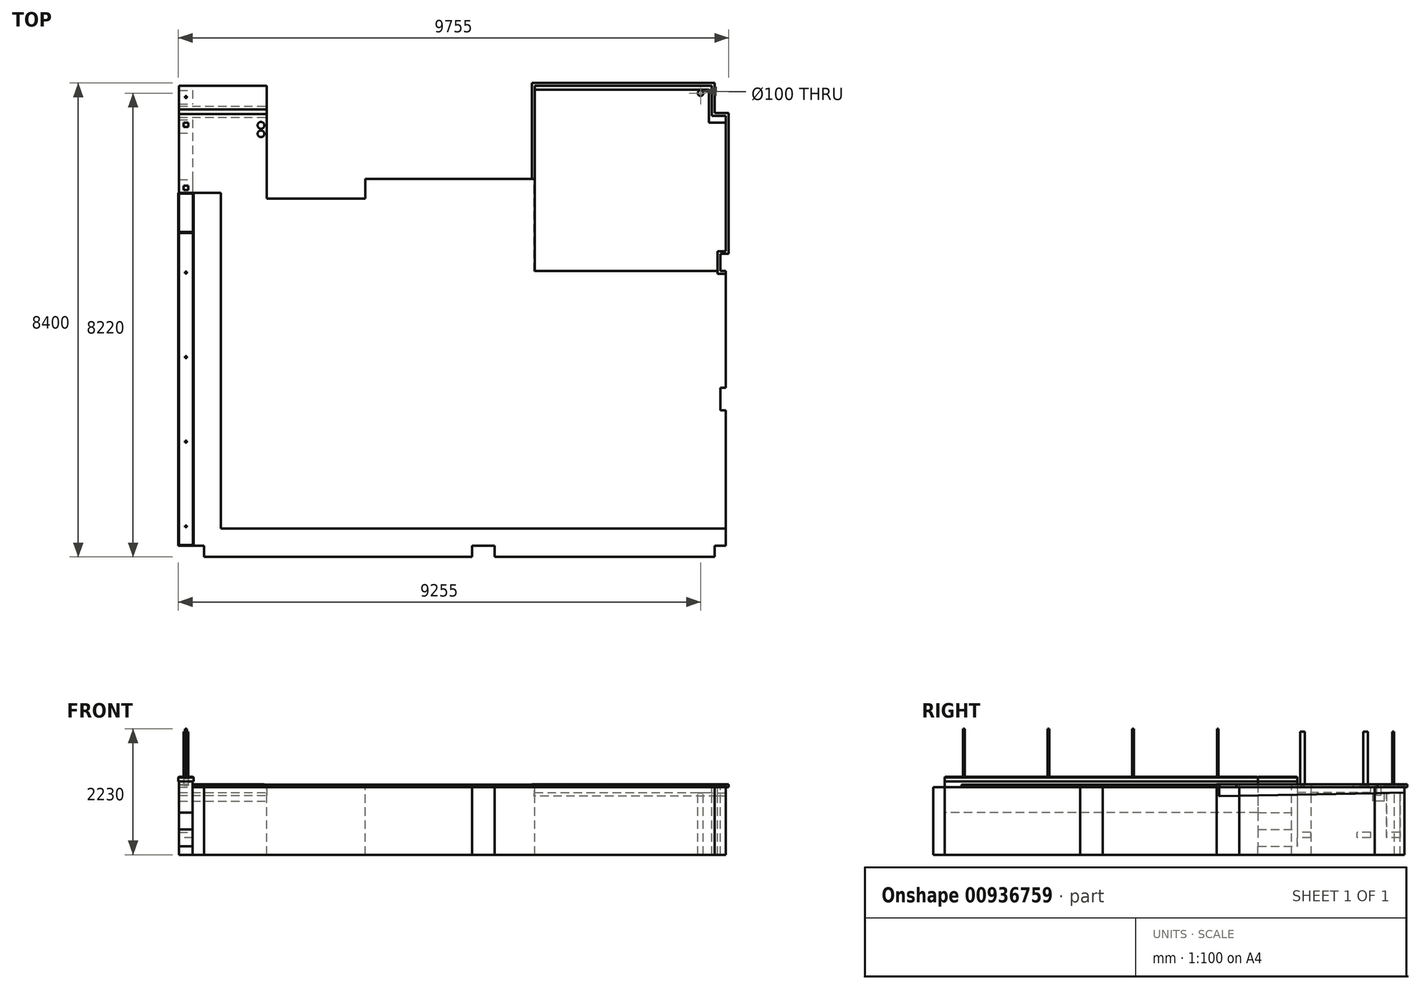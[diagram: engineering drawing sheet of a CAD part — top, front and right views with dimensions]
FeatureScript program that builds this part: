
annotation { "Feature Type Name" : "Feature", "Feature Type Description" : "" }
export const myFeature = defineFeature(function(context is Context, id is Id, definition is map)
    precondition{}
    {
        {
            var Q0;
            Q0=qCreatedBy(makeId("Top.planeOp"),FACE);
            var sketch = newSketch(context, id + "F0", { "sketchPlane" : qUnion([Q0])});
            skLineSegment(sketch, "E0", {"start": v(-250, 0) * mm, "end": v(0, 0) * mm, "construction": true});
            skLineSegment(sketch, "E1", {"start": v(0, 0) * mm, "end": v(0, -530) * mm, "construction": true});
            skCircle(sketch, "E2", {"center": v(-450, -130) * mm, "radius": 50 * mm});
            skLineSegment(sketch, "E3", {"start": v(-250, 0) * mm, "end": v(-250, -530) * mm});
            skLineSegment(sketch, "E4", {"start": v(-250, -530) * mm, "end": v(0, -530) * mm});
            skLineSegment(sketch, "E5", {"start": v(-250, 0) * mm, "end": v(-3390, 0) * mm});
            skLineSegment(sketch, "E6", {"start": v(0, -530) * mm, "end": v(0, -2930) * mm});
            skLineSegment(sketch, "E7", {"start": v(-3390, 0) * mm, "end": v(-3390, -1650) * mm});
            skLineSegment(sketch, "E8", {"start": v(0, -2930) * mm, "end": v(-150, -2930) * mm});
            skLineSegment(sketch, "E9", {"start": v(-150, -2930) * mm, "end": v(-150, -3330) * mm});
            skLineSegment(sketch, "E10", {"start": v(-150, -3330) * mm, "end": v(0, -3330) * mm});
            skLineSegment(sketch, "E11", {"start": v(-3390, -70) * mm, "end": v(-250, -70) * mm, "construction": true});
            skLineSegment(sketch, "E12", {"start": v(-300, -70) * mm, "end": v(-300, -650) * mm, "construction": true});
            skLineSegment(sketch, "E13", {"start": v(-300, -650) * mm, "end": v(0, -650) * mm, "construction": true});
            skLineSegment(sketch, "E14", {"start": v(-3390, -1650) * mm, "end": v(-6390, -1650) * mm});
            skLineSegment(sketch, "E15", {"start": v(-6390, -1650) * mm, "end": v(-6390, -2000) * mm});
            skLineSegment(sketch, "E16", {"start": v(-6390, -2000) * mm, "end": v(-8140, -2000) * mm});
            skLineSegment(sketch, "E17", {"start": v(-8140, -2000) * mm, "end": v(-8140, 0) * mm});
            skLineSegment(sketch, "E18", {"start": v(-8140, 0) * mm, "end": v(-9690, 0) * mm});
            skLineSegment(sketch, "E19", {"start": v(-9690, 0) * mm, "end": v(-9690, -2600) * mm});
            skLineSegment(sketch, "E20", {"start": v(-9450, -2600) * mm, "end": v(-9450, -8150) * mm});
            skLineSegment(sketch, "E21", {"start": v(-9450, -8150) * mm, "end": v(-9250, -8150) * mm});
            skLineSegment(sketch, "E22", {"start": v(-9250, -8150) * mm, "end": v(-9250, -8350) * mm});
            skLineSegment(sketch, "E23", {"start": v(-9250, -8350) * mm, "end": v(-4500, -8350) * mm});
            skLineSegment(sketch, "E24", {"start": v(-4500, -8350) * mm, "end": v(-4500, -8150) * mm});
            skLineSegment(sketch, "E25", {"start": v(-4500, -8150) * mm, "end": v(-4100, -8150) * mm});
            skLineSegment(sketch, "E26", {"start": v(0, -3330) * mm, "end": v(0, -5350) * mm});
            skLineSegment(sketch, "E27", {"start": v(0, -5350) * mm, "end": v(-100, -5350) * mm});
            skLineSegment(sketch, "E28", {"start": v(-100, -5350) * mm, "end": v(-100, -5750) * mm});
            skLineSegment(sketch, "E29", {"start": v(-100, -5750) * mm, "end": v(0, -5750) * mm});
            skLineSegment(sketch, "E30", {"start": v(0, -5750) * mm, "end": v(0, -8150) * mm});
            skLineSegment(sketch, "E31", {"start": v(0, -8150) * mm, "end": v(-200, -8150) * mm});
            skLineSegment(sketch, "E32", {"start": v(-200, -8150) * mm, "end": v(-200, -8350) * mm});
            skLineSegment(sketch, "E33", {"start": v(-200, -8350) * mm, "end": v(-4100, -8350) * mm});
            skLineSegment(sketch, "E34", {"start": v(-4100, -8150) * mm, "end": v(-4100, -8350) * mm});
            skLineSegment(sketch, "E35", {"start": v(-9690, -2600) * mm, "end": v(-9450, -2600) * mm});
            skSolve(sketch);
        }
        {
            var Q0;
            Q0=qCreatedBy(makeId("Top.planeOp"),FACE);
            var sketch = newSketch(context, id + "F1", { "sketchPlane" : qUnion([Q0])});
            skLineSegment(sketch, "E36.0", {"start": v(-3390, 0) * mm, "end": v(-3390, -1650) * mm});
            skLineSegment(sketch, "E36.1", {"start": v(-250, 0) * mm, "end": v(-3390, 0) * mm});
            skLineSegment(sketch, "E36.2", {"start": v(-250, 0) * mm, "end": v(-250, -530) * mm});
            skLineSegment(sketch, "E36.3", {"start": v(-250, -530) * mm, "end": v(0, -530) * mm});
            skLineSegment(sketch, "E36.4", {"start": v(0, -530) * mm, "end": v(0, -2930) * mm});
            skLineSegment(sketch, "E36.5", {"start": v(0, -2930) * mm, "end": v(-150, -2930) * mm});
            skLineSegment(sketch, "E36.6", {"start": v(-150, -2930) * mm, "end": v(-150, -3330) * mm});
            skLineSegment(sketch, "E36.7", {"start": v(-150, -3330) * mm, "end": v(0, -3330) * mm});
            skLineSegment(sketch, "E37.0", {"start": v(-3440, 50) * mm, "end": v(-3440, -1650) * mm});
            skLineSegment(sketch, "E37.1", {"start": v(-200, 50) * mm, "end": v(-3440, 50) * mm});
            skLineSegment(sketch, "E37.2", {"start": v(-200, 50) * mm, "end": v(-200, -480) * mm});
            skLineSegment(sketch, "E37.3", {"start": v(-200, -480) * mm, "end": v(50, -480) * mm});
            skLineSegment(sketch, "E37.4", {"start": v(-100, -3280) * mm, "end": v(0, -3280) * mm});
            skLineSegment(sketch, "E37.5", {"start": v(-100, -2980) * mm, "end": v(-100, -3280) * mm});
            skLineSegment(sketch, "E37.6", {"start": v(50, -2980) * mm, "end": v(-100, -2980) * mm});
            skLineSegment(sketch, "E37.7", {"start": v(50, -480) * mm, "end": v(50, -2980) * mm});
            skLineSegment(sketch, "E38", {"start": v(-3390, -1650) * mm, "end": v(-3440, -1650) * mm});
            skLineSegment(sketch, "E39", {"start": v(0, -3330) * mm, "end": v(0, -3280) * mm});
            skCircle(sketch, "E40.0", {"center": v(-450, -130) * mm, "radius": 50 * mm});
            skSolve(sketch);
        }
        {
            var Q0;
            Q0=qSketchRegion(id+"F1",true);
            extrude(context, id + "F2", {"entities" : qUnion([Q0]), "depth" : 50 * mm, "offsetDistance" : 25 * mm});
        }
        {
            var Q0;
            Q0=qCreatedBy(makeId("Top.planeOp"),FACE);
            var sketch = newSketch(context, id + "F3", { "sketchPlane" : qUnion([Q0])});
            skLineSegment(sketch, "E41.0", {"start": v(-3390, -70) * mm, "end": v(-300, -70) * mm});
            skLineSegment(sketch, "E41.1", {"start": v(-250, 0) * mm, "end": v(-3390, 0) * mm});
            skLineSegment(sketch, "E41.2", {"start": v(-3390, 0) * mm, "end": v(-3390, -70) * mm});
            skLineSegment(sketch, "E41.3", {"start": v(-300, -70) * mm, "end": v(-300, -650) * mm});
            skLineSegment(sketch, "E41.4", {"start": v(-250, 0) * mm, "end": v(-250, -530) * mm});
            skLineSegment(sketch, "E41.5", {"start": v(-300, -650) * mm, "end": v(0, -650) * mm});
            skLineSegment(sketch, "E41.6", {"start": v(-250, -530) * mm, "end": v(0, -530) * mm});
            skLineSegment(sketch, "E41.7", {"start": v(0, -530) * mm, "end": v(0, -650) * mm});
            skPoint(sketch, "E42.orphan", {"position": v(-250, -70) * mm});
            skPoint(sketch, "E43.orphan", {"position": v(0, -2930) * mm});
            skPoint(sketch, "E44.orphan", {"position": v(-3390, -1650) * mm});
            skSolve(sketch);
        }
        {
            var Q0;
            Q0=qSketchRegion(id+"F3",true);
            extrude(context, id + "F4", {"entities" : qUnion([Q0]), "depth" : 1 * mm, "offsetDistance" : 25 * mm});
        }
        {
            var Q0;
            Q0 = qSketchRegion(id + "F0", true);
            extrude(context, id + "F5", {"entities" : qUnion([Q0]), "oppositeDirection" : true, "depth" : 1200 * mm, "offsetDistance" : 25 * mm});
        }
        {
            var Q0;
            Q0=qCreatedBy(makeId("Top.planeOp"),FACE);
            var sketch = newSketch(context, id + "F6", { "sketchPlane" : qUnion([Q0])});
            skLineSegment(sketch, "E45.bottom", {"start": v(-9690, -2600) * mm, "end": v(-9450, -2600) * mm});
            skLineSegment(sketch, "E45.top", {"start": v(-9690, -8150) * mm, "end": v(-9450, -8150) * mm});
            skLineSegment(sketch, "E45.left", {"start": v(-9690, -2600) * mm, "end": v(-9690, -8150) * mm});
            skLineSegment(sketch, "E45.right", {"start": v(-9450, -2600) * mm, "end": v(-9450, -8150) * mm});
            skSolve(sketch);
        }
        {
            var Q0;
            Q0 = qSketchRegion(id + "F6", true);
            extrude(context, id + "F7", {"entities" : qUnion([Q0]), "depth" : 100 * mm, "offsetDistance" : 25 * mm, "hasSecondDirection" : true, "secondDirectionOppositeDirection" : true, "secondDirectionDepth" : 450 * mm});
        }
        {
            var Q0;
            Q0=makeQuery(id+"F0.imprint","IMPRINT",FACE,{"disambiguationData":[TD([[makeQuery(id+"F0.imprint","IMPRINT",EDGE,{"derivedFrom":sQuery(id+"F0.wireOp",EDGE,"E2")}),-1.0]])]});
            var sketch = newSketch(context, id + "F8", { "sketchPlane" : qUnion([Q0])});
            skLineSegment(sketch, "E46", {"start": v(-3390, -1650) * mm, "end": v(-3390, -3282) * mm});
            skLineSegment(sketch, "E47", {"start": v(-3390, -3282) * mm, "end": v(-150, -3282) * mm});
            skLineSegment(sketch, "E48.0", {"start": v(-150, -2930) * mm, "end": v(-150, -3282) * mm});
            skLineSegment(sketch, "E48.1", {"start": v(0, -2930) * mm, "end": v(-150, -2930) * mm});
            skLineSegment(sketch, "E48.2", {"start": v(0, -530) * mm, "end": v(0, -2930) * mm});
            skLineSegment(sketch, "E48.3", {"start": v(-250, -530) * mm, "end": v(0, -530) * mm});
            skLineSegment(sketch, "E48.4", {"start": v(-250, 0) * mm, "end": v(-250, -530) * mm});
            skLineSegment(sketch, "E48.5", {"start": v(-250, 0) * mm, "end": v(-3390, 0) * mm});
            skLineSegment(sketch, "E49.0", {"start": v(-3390, 0) * mm, "end": v(-3390, -1650) * mm});
            skSolve(sketch);
        }
        {
            var Q0;
            Q0=makeQuery(id+"F5.opExtrude","SWEPT_FACE",FACE,{"disambiguationData":[OSD([sQuery(id+"F0.wireOp",EDGE,"E9")])]});
            var sketch = newSketch(context, id + "F9", { "sketchPlane" : qUnion([Q0])});
            skLineSegment(sketch, "E50", {"start": v(-3282, 0) * mm, "end": v(-3282, -160) * mm});
            skLineSegment(sketch, "E51", {"start": v(-3282, -160) * mm, "end": v(0, -100) * mm});
            skLineSegment(sketch, "E52", {"start": v(0, -100) * mm, "end": v(0, 0) * mm});
            skSolve(sketch);
        }
        {
            var Q0;
            Q0=sQuery(id+"F9.wireOp",EDGE,"E51");
            cPlane(context, id + "F10", {"entities" : qUnion([Q0]), "cplaneType" : CPlaneType.LINE_ANGLE, "offset" : 25 * mm, "angle" : 0 * degree, "width" : 150 * mm, "height" : 150 * mm});
        }
        {
            var Q0;
            Q0 = qSketchRegion(id + "F8", true);
            var Q1;
            Q1=qCreatedBy(id+"F10.planeOp",FACE);
            var Q2;
            Q2=makeQuery(id+"F5.opExtrude","CAP_VERTEX",VERTEX,{"disambiguationData":[OSD([sQuery(id+"F0.wireOp",EDGE,"E6"),sQuery(id+"F0.wireOp",EDGE,"E8")])],"isStart":false});
            extrude(context, id + "F11", {"entities" : qUnion([Q0]), "operationType" : NewBodyOperationType.REMOVE, "endBound" : BoundingType.UP_TO_SURFACE, "oppositeDirection" : true, "depth" : 360 * mm, "endBoundEntityFace" : qUnion([Q1]), "endBoundEntityVertex" : qUnion([Q2]), "offsetDistance" : 25 * mm, "hasDraft" : true, "draftAngle" : 3 * degree});
        }
        {
            var Q0;
            Q0 = qSketchRegion(id + "F8", true);
            var Q1;
            Q1=makeQuery(id+"F11.boolean.opBoolean","COPY",FACE,{"derivedFrom":makeQuery(id+"F11.opExtrude","CAP_FACE",FACE,{"disambiguationData":[OSD([sQuery(id+"F8.wireOp",EDGE,"E46"),sQuery(id+"F8.wireOp",EDGE,"E47"),sQuery(id+"F8.wireOp",EDGE,"E48.0"),sQuery(id+"F8.wireOp",EDGE,"E48.1"),sQuery(id+"F8.wireOp",EDGE,"E48.2"),sQuery(id+"F8.wireOp",EDGE,"E48.3"),sQuery(id+"F8.wireOp",EDGE,"E48.4"),sQuery(id+"F8.wireOp",EDGE,"E48.5"),sQuery(id+"F8.wireOp",EDGE,"E49.0")])],"isStart":false})});
            extrude(context, id + "F12", {"entities" : qUnion([Q0]), "endBound" : BoundingType.UP_TO_SURFACE, "oppositeDirection" : true, "depth" : 25 * mm, "endBoundEntityFace" : qUnion([Q1]), "offsetDistance" : 25 * mm});
        }
        {
            var Q0;
            Q0=makeQuery(id+"F5.opExtrude","CAP_FACE",FACE,{"disambiguationData":[OSD([sQuery(id+"F0.wireOp",EDGE,"E2"),sQuery(id+"F0.wireOp",EDGE,"E3"),sQuery(id+"F0.wireOp",EDGE,"E4"),sQuery(id+"F0.wireOp",EDGE,"E5"),sQuery(id+"F0.wireOp",EDGE,"E6"),sQuery(id+"F0.wireOp",EDGE,"E7"),sQuery(id+"F0.wireOp",EDGE,"E8"),sQuery(id+"F0.wireOp",EDGE,"E9"),sQuery(id+"F0.wireOp",EDGE,"E10"),sQuery(id+"F0.wireOp",EDGE,"E14"),sQuery(id+"F0.wireOp",EDGE,"E15"),sQuery(id+"F0.wireOp",EDGE,"E16"),sQuery(id+"F0.wireOp",EDGE,"E17"),sQuery(id+"F0.wireOp",EDGE,"E18"),sQuery(id+"F0.wireOp",EDGE,"E19"),sQuery(id+"F0.wireOp",EDGE,"b0Gpvn7v-ytsP-87oV-qQFu-qrhvEngnIZt2"),sQuery(id+"F0.wireOp",EDGE,"E20"),sQuery(id+"F0.wireOp",EDGE,"E21"),sQuery(id+"F0.wireOp",EDGE,"E22"),sQuery(id+"F0.wireOp",EDGE,"E23"),sQuery(id+"F0.wireOp",EDGE,"E24"),sQuery(id+"F0.wireOp",EDGE,"E25"),sQuery(id+"F0.wireOp",EDGE,"E26"),sQuery(id+"F0.wireOp",EDGE,"E27"),sQuery(id+"F0.wireOp",EDGE,"E28"),sQuery(id+"F0.wireOp",EDGE,"E29"),sQuery(id+"F0.wireOp",EDGE,"E30"),sQuery(id+"F0.wireOp",EDGE,"E31"),sQuery(id+"F0.wireOp",EDGE,"E32"),sQuery(id+"F0.wireOp",EDGE,"E33"),sQuery(id+"F0.wireOp",EDGE,"E34")])],"isStart":true});
            var sketch = newSketch(context, id + "F13", { "sketchPlane" : qUnion([Q0])});
            skLineSegment(sketch, "E53.bottom", {"start": v(-9690, -360) * mm, "end": v(-8140, -360) * mm});
            skLineSegment(sketch, "E53.top", {"start": v(-9690, -560) * mm, "end": v(-8140, -560) * mm});
            skLineSegment(sketch, "E53.left", {"start": v(-9690, -360) * mm, "end": v(-9690, -560) * mm});
            skLineSegment(sketch, "E53.right", {"start": v(-8140, -360) * mm, "end": v(-8140, -560) * mm});
            skLineSegment(sketch, "E54", {"start": v(-9690, -420) * mm, "end": v(-8140, -420) * mm, "construction": true});
            skLineSegment(sketch, "E55", {"start": v(-9690, -500) * mm, "end": v(-8140, -500) * mm, "construction": true});
            skLineSegment(sketch, "E56", {"start": v(-8915, -360) * mm, "end": v(-8915, -420) * mm, "construction": true});
            skLineSegment(sketch, "E57", {"start": v(-8915, -420) * mm, "end": v(-8915, -500) * mm, "construction": true});
            skLineSegment(sketch, "E58", {"start": v(-8915, -500) * mm, "end": v(-8915, -560) * mm, "construction": true});
            skSolve(sketch);
        }
        {
            var Q0;
            Q0 = qSketchRegion(id + "F13", true);
            extrude(context, id + "F14", {"entities" : qUnion([Q0]), "operationType" : NewBodyOperationType.REMOVE, "oppositeDirection" : true, "depth" : 250 * mm, "offsetDistance" : 25 * mm});
        }
        {
            var Q0;
            {var subQ0=sQuery(id+"F0.wireOp",EDGE,"E17");var subQ1=sQuery(id+"F0.wireOp",EDGE,"E18");var subQ2=sQuery(id+"F0.wireOp",EDGE,"E19");Q0=makeQuery(id+"F14.boolean.opBoolean","SPLIT",FACE,{"disambiguationData":[TD([makeQuery(id+"F5.opExtrude","SWEPT_FACE",FACE,{"disambiguationData":[OSD([subQ1])]})])],"derivedFrom":makeQuery(id+"F5.opExtrude","CAP_FACE",FACE,{"disambiguationData":[OSD([sQuery(id+"F0.wireOp",EDGE,"E2"),sQuery(id+"F0.wireOp",EDGE,"E3"),sQuery(id+"F0.wireOp",EDGE,"E4"),sQuery(id+"F0.wireOp",EDGE,"E5"),sQuery(id+"F0.wireOp",EDGE,"E6"),sQuery(id+"F0.wireOp",EDGE,"E7"),sQuery(id+"F0.wireOp",EDGE,"E8"),sQuery(id+"F0.wireOp",EDGE,"E9"),sQuery(id+"F0.wireOp",EDGE,"E10"),sQuery(id+"F0.wireOp",EDGE,"E14"),sQuery(id+"F0.wireOp",EDGE,"E15"),sQuery(id+"F0.wireOp",EDGE,"E16"),subQ0,subQ1,subQ2,sQuery(id+"F0.wireOp",EDGE,"b0Gpvn7v-ytsP-87oV-qQFu-qrhvEngnIZt2"),sQuery(id+"F0.wireOp",EDGE,"E20"),sQuery(id+"F0.wireOp",EDGE,"E21"),sQuery(id+"F0.wireOp",EDGE,"E22"),sQuery(id+"F0.wireOp",EDGE,"E23"),sQuery(id+"F0.wireOp",EDGE,"E24"),sQuery(id+"F0.wireOp",EDGE,"E25"),sQuery(id+"F0.wireOp",EDGE,"E26"),sQuery(id+"F0.wireOp",EDGE,"E27"),sQuery(id+"F0.wireOp",EDGE,"E28"),sQuery(id+"F0.wireOp",EDGE,"E29"),sQuery(id+"F0.wireOp",EDGE,"E30"),sQuery(id+"F0.wireOp",EDGE,"E31"),sQuery(id+"F0.wireOp",EDGE,"E32"),sQuery(id+"F0.wireOp",EDGE,"E33"),sQuery(id+"F0.wireOp",EDGE,"E34")])],"isStart":true})});}
            extrude(context, id + "F15", {"entities" : qUnion([Q0]), "operationType" : NewBodyOperationType.REMOVE, "oppositeDirection" : true, "depth" : 100 * mm, "offsetDistance" : 25 * mm});
        }
        {
            var Q0;
            {var subQ0=sQuery(id+"F0.wireOp",EDGE,"E34");var subQ1=sQuery(id+"F0.wireOp",EDGE,"E33");var subQ2=sQuery(id+"F0.wireOp",EDGE,"E32");var subQ3=sQuery(id+"F0.wireOp",EDGE,"E31");var subQ4=sQuery(id+"F0.wireOp",EDGE,"E30");var subQ5=sQuery(id+"F0.wireOp",EDGE,"E29");var subQ6=sQuery(id+"F0.wireOp",EDGE,"E28");var subQ7=sQuery(id+"F0.wireOp",EDGE,"E27");var subQ8=sQuery(id+"F0.wireOp",EDGE,"E26");var subQ9=sQuery(id+"F0.wireOp",EDGE,"E25");var subQ10=sQuery(id+"F0.wireOp",EDGE,"E24");var subQ11=sQuery(id+"F0.wireOp",EDGE,"E23");var subQ12=sQuery(id+"F0.wireOp",EDGE,"E15");var subQ13=sQuery(id+"F0.wireOp",EDGE,"E14");var subQ14=sQuery(id+"F0.wireOp",EDGE,"E10");var subQ15=sQuery(id+"F0.wireOp",EDGE,"E9");var subQ16=sQuery(id+"F0.wireOp",EDGE,"E16");var subQ17=sQuery(id+"F0.wireOp",EDGE,"E17");var subQ18=sQuery(id+"F0.wireOp",EDGE,"E19");var subQ19=sQuery(id+"F0.wireOp",EDGE,"E20");var subQ20=sQuery(id+"F0.wireOp",EDGE,"E21");var subQ21=sQuery(id+"F0.wireOp",EDGE,"E22");var subQ22=sQuery(id+"F0.wireOp",EDGE,"E35");Q0=makeQuery(id+"F14.boolean.opBoolean","SPLIT",FACE,{"disambiguationData":[TD([makeQuery(id+"F5.opExtrude","SWEPT_FACE",FACE,{"disambiguationData":[OSD([subQ15])]})])],"derivedFrom":makeQuery(id+"F5.opExtrude","CAP_FACE",FACE,{"disambiguationData":[OSD([sQuery(id+"F0.wireOp",EDGE,"E2"),sQuery(id+"F0.wireOp",EDGE,"E3"),sQuery(id+"F0.wireOp",EDGE,"E4"),sQuery(id+"F0.wireOp",EDGE,"E5"),sQuery(id+"F0.wireOp",EDGE,"E6"),sQuery(id+"F0.wireOp",EDGE,"E7"),sQuery(id+"F0.wireOp",EDGE,"E8"),subQ15,subQ14,subQ13,subQ12,subQ16,subQ17,sQuery(id+"F0.wireOp",EDGE,"E18"),subQ18,subQ19,subQ20,subQ21,subQ11,subQ10,subQ9,subQ8,subQ7,subQ6,subQ5,subQ4,subQ3,subQ2,subQ1,subQ0,subQ22])],"isStart":true})});}
            var sketch = newSketch(context, id + "F16", { "sketchPlane" : qUnion([Q0])});
            skLineSegment(sketch, "E59.bottom", {"start": v(-9450, -2600) * mm, "end": v(-9690, -2600) * mm});
            skLineSegment(sketch, "E59.top", {"start": v(-9450, -1900) * mm, "end": v(-9690, -1900) * mm});
            skLineSegment(sketch, "E59.left", {"start": v(-9450, -2600) * mm, "end": v(-9450, -1900) * mm});
            skLineSegment(sketch, "E59.right", {"start": v(-9690, -2600) * mm, "end": v(-9690, -1900) * mm});
            skSolve(sketch);
        }
        {
            var Q0;
            Q0 = qSketchRegion(id + "F16", true);
            extrude(context, id + "F17", {"entities" : qUnion([Q0]), "operationType" : NewBodyOperationType.REMOVE, "oppositeDirection" : true, "depth" : 1050 * mm, "offsetDistance" : 25 * mm});
        }
        {
            var Q0;
            {var subQ0=sQuery(id+"F0.wireOp",EDGE,"E34");var subQ1=sQuery(id+"F0.wireOp",EDGE,"E33");var subQ2=sQuery(id+"F0.wireOp",EDGE,"E32");var subQ3=sQuery(id+"F0.wireOp",EDGE,"E31");var subQ4=sQuery(id+"F0.wireOp",EDGE,"E30");var subQ5=sQuery(id+"F0.wireOp",EDGE,"E29");var subQ6=sQuery(id+"F0.wireOp",EDGE,"E28");var subQ7=sQuery(id+"F0.wireOp",EDGE,"E27");var subQ8=sQuery(id+"F0.wireOp",EDGE,"E26");var subQ9=sQuery(id+"F0.wireOp",EDGE,"E25");var subQ10=sQuery(id+"F0.wireOp",EDGE,"E24");var subQ11=sQuery(id+"F0.wireOp",EDGE,"E23");var subQ12=sQuery(id+"F0.wireOp",EDGE,"E15");var subQ13=sQuery(id+"F0.wireOp",EDGE,"E14");var subQ14=sQuery(id+"F0.wireOp",EDGE,"E10");var subQ15=sQuery(id+"F0.wireOp",EDGE,"E9");var subQ16=sQuery(id+"F0.wireOp",EDGE,"E16");var subQ17=sQuery(id+"F0.wireOp",EDGE,"E17");var subQ18=sQuery(id+"F0.wireOp",EDGE,"E19");var subQ19=sQuery(id+"F0.wireOp",EDGE,"E20");var subQ20=sQuery(id+"F0.wireOp",EDGE,"E21");var subQ21=sQuery(id+"F0.wireOp",EDGE,"E22");var subQ22=sQuery(id+"F0.wireOp",EDGE,"E35");Q0=makeQuery(id+"F14.boolean.opBoolean","SPLIT",FACE,{"disambiguationData":[TD([makeQuery(id+"F5.opExtrude","SWEPT_FACE",FACE,{"disambiguationData":[OSD([subQ15])]})])],"derivedFrom":makeQuery(id+"F5.opExtrude","CAP_FACE",FACE,{"disambiguationData":[OSD([sQuery(id+"F0.wireOp",EDGE,"E2"),sQuery(id+"F0.wireOp",EDGE,"E3"),sQuery(id+"F0.wireOp",EDGE,"E4"),sQuery(id+"F0.wireOp",EDGE,"E5"),sQuery(id+"F0.wireOp",EDGE,"E6"),sQuery(id+"F0.wireOp",EDGE,"E7"),sQuery(id+"F0.wireOp",EDGE,"E8"),subQ15,subQ14,subQ13,subQ12,subQ16,subQ17,sQuery(id+"F0.wireOp",EDGE,"E18"),subQ18,subQ19,subQ20,subQ21,subQ11,subQ10,subQ9,subQ8,subQ7,subQ6,subQ5,subQ4,subQ3,subQ2,subQ1,subQ0,subQ22])],"isStart":true})});}
            var sketch = newSketch(context, id + "F18", { "sketchPlane" : qUnion([Q0])});
            skLineSegment(sketch, "E60.bottom", {"start": v(-9690, -600) * mm, "end": v(-9450, -600) * mm});
            skLineSegment(sketch, "E60.top", {"start": v(-9690, -840) * mm, "end": v(-9450, -840) * mm});
            skLineSegment(sketch, "E60.left", {"start": v(-9690, -600) * mm, "end": v(-9690, -840) * mm});
            skLineSegment(sketch, "E60.right", {"start": v(-9450, -600) * mm, "end": v(-9450, -840) * mm});
            skLineSegment(sketch, "E61.bottom", {"start": v(-9690, -1660) * mm, "end": v(-9450, -1660) * mm});
            skLineSegment(sketch, "E61.top", {"start": v(-9690, -1900) * mm, "end": v(-9450, -1900) * mm});
            skLineSegment(sketch, "E61.left", {"start": v(-9690, -1660) * mm, "end": v(-9690, -1900) * mm});
            skLineSegment(sketch, "E61.right", {"start": v(-9450, -1660) * mm, "end": v(-9450, -1900) * mm});
            skSolve(sketch);
        }
        {
            var Q0;
            Q0 = qSketchRegion(id + "F18", true);
            extrude(context, id + "F19", {"entities" : qUnion([Q0]), "operationType" : NewBodyOperationType.REMOVE, "oppositeDirection" : true, "depth" : 900 * mm, "offsetDistance" : 25 * mm});
        }
        {
            var Q0;
            {var subQ0=sQuery(id+"F0.wireOp",EDGE,"E34");var subQ1=sQuery(id+"F0.wireOp",EDGE,"E33");var subQ2=sQuery(id+"F0.wireOp",EDGE,"E32");var subQ3=sQuery(id+"F0.wireOp",EDGE,"E31");var subQ4=sQuery(id+"F0.wireOp",EDGE,"E30");var subQ5=sQuery(id+"F0.wireOp",EDGE,"E29");var subQ6=sQuery(id+"F0.wireOp",EDGE,"E28");var subQ7=sQuery(id+"F0.wireOp",EDGE,"E27");var subQ8=sQuery(id+"F0.wireOp",EDGE,"E26");var subQ9=sQuery(id+"F0.wireOp",EDGE,"E25");var subQ10=sQuery(id+"F0.wireOp",EDGE,"E24");var subQ11=sQuery(id+"F0.wireOp",EDGE,"E23");var subQ12=sQuery(id+"F0.wireOp",EDGE,"E15");var subQ13=sQuery(id+"F0.wireOp",EDGE,"E14");var subQ14=sQuery(id+"F0.wireOp",EDGE,"E10");var subQ15=sQuery(id+"F0.wireOp",EDGE,"E9");var subQ16=sQuery(id+"F0.wireOp",EDGE,"E16");var subQ17=sQuery(id+"F0.wireOp",EDGE,"E17");var subQ18=sQuery(id+"F0.wireOp",EDGE,"E19");var subQ19=sQuery(id+"F0.wireOp",EDGE,"E20");var subQ20=sQuery(id+"F0.wireOp",EDGE,"E21");var subQ21=sQuery(id+"F0.wireOp",EDGE,"E22");var subQ22=sQuery(id+"F0.wireOp",EDGE,"E35");Q0=makeQuery(id+"F14.boolean.opBoolean","SPLIT",FACE,{"disambiguationData":[TD([makeQuery(id+"F5.opExtrude","SWEPT_FACE",FACE,{"disambiguationData":[OSD([subQ15])]})])],"derivedFrom":makeQuery(id+"F5.opExtrude","CAP_FACE",FACE,{"disambiguationData":[OSD([sQuery(id+"F0.wireOp",EDGE,"E2"),sQuery(id+"F0.wireOp",EDGE,"E3"),sQuery(id+"F0.wireOp",EDGE,"E4"),sQuery(id+"F0.wireOp",EDGE,"E5"),sQuery(id+"F0.wireOp",EDGE,"E6"),sQuery(id+"F0.wireOp",EDGE,"E7"),sQuery(id+"F0.wireOp",EDGE,"E8"),subQ15,subQ14,subQ13,subQ12,subQ16,subQ17,sQuery(id+"F0.wireOp",EDGE,"E18"),subQ18,subQ19,subQ20,subQ21,subQ11,subQ10,subQ9,subQ8,subQ7,subQ6,subQ5,subQ4,subQ3,subQ2,subQ1,subQ0,subQ22])],"isStart":true})});}
            var sketch = newSketch(context, id + "F20", { "sketchPlane" : qUnion([Q0])});
            skLineSegment(sketch, "E62.bottom", {"start": v(-9690, -840) * mm, "end": v(-9450, -840) * mm});
            skLineSegment(sketch, "E62.top", {"start": v(-9690, -1660) * mm, "end": v(-9450, -1660) * mm});
            skLineSegment(sketch, "E62.left", {"start": v(-9690, -840) * mm, "end": v(-9690, -1660) * mm});
            skLineSegment(sketch, "E62.right", {"start": v(-9450, -840) * mm, "end": v(-9450, -1660) * mm});
            skSolve(sketch);
        }
        {
            var Q0;
            Q0 = qSketchRegion(id + "F20", true);
            extrude(context, id + "F21", {"entities" : qUnion([Q0]), "operationType" : NewBodyOperationType.REMOVE, "oppositeDirection" : true, "depth" : 400 * mm, "offsetDistance" : 25 * mm});
        }
        {
            var Q0;
            {var subQ0=sQuery(id+"F0.wireOp",EDGE,"E34");var subQ1=sQuery(id+"F0.wireOp",EDGE,"E33");var subQ2=sQuery(id+"F0.wireOp",EDGE,"E32");var subQ3=sQuery(id+"F0.wireOp",EDGE,"E31");var subQ4=sQuery(id+"F0.wireOp",EDGE,"E30");var subQ5=sQuery(id+"F0.wireOp",EDGE,"E29");var subQ6=sQuery(id+"F0.wireOp",EDGE,"E28");var subQ7=sQuery(id+"F0.wireOp",EDGE,"E27");var subQ8=sQuery(id+"F0.wireOp",EDGE,"E26");var subQ9=sQuery(id+"F0.wireOp",EDGE,"E25");var subQ10=sQuery(id+"F0.wireOp",EDGE,"E24");var subQ11=sQuery(id+"F0.wireOp",EDGE,"E23");var subQ12=sQuery(id+"F0.wireOp",EDGE,"E15");var subQ13=sQuery(id+"F0.wireOp",EDGE,"E14");var subQ14=sQuery(id+"F0.wireOp",EDGE,"E10");var subQ15=sQuery(id+"F0.wireOp",EDGE,"E9");var subQ16=sQuery(id+"F0.wireOp",EDGE,"E16");var subQ17=sQuery(id+"F0.wireOp",EDGE,"E17");var subQ18=sQuery(id+"F0.wireOp",EDGE,"E19");var subQ19=sQuery(id+"F0.wireOp",EDGE,"E20");var subQ20=sQuery(id+"F0.wireOp",EDGE,"E21");var subQ21=sQuery(id+"F0.wireOp",EDGE,"E22");var subQ22=sQuery(id+"F0.wireOp",EDGE,"E35");Q0=makeQuery(id+"F14.boolean.opBoolean","SPLIT",FACE,{"disambiguationData":[TD([makeQuery(id+"F5.opExtrude","SWEPT_FACE",FACE,{"disambiguationData":[OSD([subQ15])]})])],"derivedFrom":makeQuery(id+"F5.opExtrude","CAP_FACE",FACE,{"disambiguationData":[OSD([sQuery(id+"F0.wireOp",EDGE,"E2"),sQuery(id+"F0.wireOp",EDGE,"E3"),sQuery(id+"F0.wireOp",EDGE,"E4"),sQuery(id+"F0.wireOp",EDGE,"E5"),sQuery(id+"F0.wireOp",EDGE,"E6"),sQuery(id+"F0.wireOp",EDGE,"E7"),sQuery(id+"F0.wireOp",EDGE,"E8"),subQ15,subQ14,subQ13,subQ12,subQ16,subQ17,sQuery(id+"F0.wireOp",EDGE,"E18"),subQ18,subQ19,subQ20,subQ21,subQ11,subQ10,subQ9,subQ8,subQ7,subQ6,subQ5,subQ4,subQ3,subQ2,subQ1,subQ0,subQ22])],"isStart":true})});}
            var sketch = newSketch(context, id + "F22", { "sketchPlane" : qUnion([Q0])});
            skLineSegment(sketch, "E63.bottom", {"start": v(-9690, -80) * mm, "end": v(-9450, -80) * mm});
            skLineSegment(sketch, "E63.top", {"start": v(-9690, -320) * mm, "end": v(-9450, -320) * mm});
            skLineSegment(sketch, "E63.left", {"start": v(-9690, -80) * mm, "end": v(-9690, -320) * mm});
            skLineSegment(sketch, "E63.right", {"start": v(-9450, -80) * mm, "end": v(-9450, -320) * mm});
            skLineSegment(sketch, "E64", {"start": v(-9690, -200) * mm, "end": v(-9450, -200) * mm, "construction": true});
            skSolve(sketch);
        }
        {
            var Q0;
            Q0 = qSketchRegion(id + "F22", true);
            extrude(context, id + "F23", {"entities" : qUnion([Q0]), "operationType" : NewBodyOperationType.REMOVE, "oppositeDirection" : true, "depth" : 900 * mm, "offsetDistance" : 25 * mm});
        }
        {
            var Q0;
            Q0=makeQuery(id+"F7.opExtrude","CAP_FACE",FACE,{"disambiguationData":[OSD([sQuery(id+"F6.wireOp",EDGE,"E45.bottom"),sQuery(id+"F6.wireOp",EDGE,"E45.top"),sQuery(id+"F6.wireOp",EDGE,"E45.left"),sQuery(id+"F6.wireOp",EDGE,"E45.right")])],"isStart":false});
            var sketch = newSketch(context, id + "F24", { "sketchPlane" : qUnion([Q0])});
            skLineSegment(sketch, "E65.bottom", {"start": v(-9705, -2600) * mm, "end": v(-9435, -2600) * mm});
            skLineSegment(sketch, "E65.top", {"start": v(-9705, -8150) * mm, "end": v(-9435, -8150) * mm});
            skLineSegment(sketch, "E65.left", {"start": v(-9705, -2600) * mm, "end": v(-9705, -8150) * mm});
            skLineSegment(sketch, "E65.right", {"start": v(-9435, -2600) * mm, "end": v(-9435, -8150) * mm});
            skLineSegment(sketch, "E66", {"start": v(-9570, -2600) * mm, "end": v(-9570, -8150) * mm, "construction": true});
            skSolve(sketch);
        }
        {
            var Q0;
            Q0 = qSketchRegion(id + "F24", true);
            extrude(context, id + "F25", {"entities" : qUnion([Q0]), "depth" : 80 * mm, "offsetDistance" : 25 * mm});
        }
        {
            var Q0;
            Q0=makeQuery(id+"F25.opExtrude","CAP_FACE",FACE,{"disambiguationData":[OSD([sQuery(id+"F24.wireOp",EDGE,"E65.bottom"),sQuery(id+"F24.wireOp",EDGE,"E65.top"),sQuery(id+"F24.wireOp",EDGE,"E65.left"),sQuery(id+"F24.wireOp",EDGE,"E65.right")])],"isStart":false});
            chamfer(context, id + "F26", {"entities" : qUnion([Q0]), "width" : 10 * mm, "tangentPropagation" : true});
        }
        {
            var Q0;
            Q0=makeQuery(id+"F17.boolean.opBoolean","COPY",FACE,{"derivedFrom":makeQuery(id+"F17.opExtrude","CAP_FACE",FACE,{"disambiguationData":[OSD([sQuery(id+"F16.wireOp",EDGE,"E59.bottom"),sQuery(id+"F16.wireOp",EDGE,"E59.top"),sQuery(id+"F16.wireOp",EDGE,"E59.left"),sQuery(id+"F16.wireOp",EDGE,"E59.right")])],"isStart":false})});
            extrude(context, id + "F27", {"entities" : qUnion([Q0]), "depth" : 300 * mm, "offsetDistance" : 25 * mm});
        }
        {
            var Q0;
            Q0=makeQuery(id+"F27.opExtrude","CAP_FACE",FACE,{"disambiguationData":[OSD([sQuery(id+"F16.wireOp",EDGE,"E59.bottom"),sQuery(id+"F16.wireOp",EDGE,"E59.top"),sQuery(id+"F16.wireOp",EDGE,"E59.left"),sQuery(id+"F16.wireOp",EDGE,"E59.right")])],"isStart":false});
            extrude(context, id + "F28", {"entities" : qUnion([Q0]), "depth" : 300 * mm, "offsetDistance" : 25 * mm});
        }
        {
            var Q0;
            Q0=makeQuery(id+"F19.boolean.opBoolean","COPY",FACE,{"derivedFrom":makeQuery(id+"F19.opExtrude","CAP_FACE",FACE,{"disambiguationData":[OSD([sQuery(id+"F18.wireOp",EDGE,"E61.bottom"),sQuery(id+"F18.wireOp",EDGE,"E61.top"),sQuery(id+"F18.wireOp",EDGE,"E61.left"),sQuery(id+"F18.wireOp",EDGE,"E61.right")])],"isStart":false})});
            var Q1;
            Q1=makeQuery(id+"F19.boolean.opBoolean","COPY",FACE,{"derivedFrom":makeQuery(id+"F19.opExtrude","CAP_FACE",FACE,{"disambiguationData":[OSD([sQuery(id+"F18.wireOp",EDGE,"E60.bottom"),sQuery(id+"F18.wireOp",EDGE,"E60.top"),sQuery(id+"F18.wireOp",EDGE,"E60.left"),sQuery(id+"F18.wireOp",EDGE,"E60.right")])],"isStart":false})});
            var Q2;
            Q2=makeQuery(id+"F23.boolean.opBoolean","COPY",FACE,{"derivedFrom":makeQuery(id+"F23.opExtrude","CAP_FACE",FACE,{"disambiguationData":[OSD([sQuery(id+"F22.wireOp",EDGE,"E63.bottom"),sQuery(id+"F22.wireOp",EDGE,"E63.top"),sQuery(id+"F22.wireOp",EDGE,"E63.left"),sQuery(id+"F22.wireOp",EDGE,"E63.right")])],"isStart":false})});
            extrude(context, id + "F29", {"entities" : qUnion([Q0, Q1, Q2]), "depth" : 100 * mm, "offsetDistance" : 25 * mm});
        }
        {
            var Q0;
            Q0=makeQuery(id+"F29.opExtrude","CAP_FACE",FACE,{"disambiguationData":[OSD([sQuery(id+"F18.wireOp",EDGE,"E61.bottom"),sQuery(id+"F18.wireOp",EDGE,"E61.top"),sQuery(id+"F18.wireOp",EDGE,"E61.left"),sQuery(id+"F18.wireOp",EDGE,"E61.right")])],"isStart":false});
            var Q1;
            Q1=makeQuery(id+"F29.opExtrude","CAP_FACE",FACE,{"disambiguationData":[OSD([sQuery(id+"F18.wireOp",EDGE,"E60.bottom"),sQuery(id+"F18.wireOp",EDGE,"E60.top"),sQuery(id+"F18.wireOp",EDGE,"E60.left"),sQuery(id+"F18.wireOp",EDGE,"E60.right")])],"isStart":false});
            var Q2;
            Q2=makeQuery(id+"F29.opExtrude","CAP_FACE",FACE,{"disambiguationData":[OSD([sQuery(id+"F22.wireOp",EDGE,"E63.bottom"),sQuery(id+"F22.wireOp",EDGE,"E63.top"),sQuery(id+"F22.wireOp",EDGE,"E63.left"),sQuery(id+"F22.wireOp",EDGE,"E63.right")])],"isStart":false});
            extrude(context, id + "F30", {"entities" : qUnion([Q0, Q1, Q2]), "depth" : 700 * mm, "offsetDistance" : 25 * mm});
        }
        {
            var Q0;
            Q0=makeQuery(id+"F21.boolean.opBoolean","COPY",FACE,{"derivedFrom":makeQuery(id+"F21.opExtrude","CAP_FACE",FACE,{"disambiguationData":[OSD([sQuery(id+"F20.wireOp",EDGE,"E62.bottom"),sQuery(id+"F20.wireOp",EDGE,"E62.top"),sQuery(id+"F20.wireOp",EDGE,"E62.left"),sQuery(id+"F20.wireOp",EDGE,"E62.right")])],"isStart":false})});
            var Q1;
            Q1=makeQuery(id+"F30.opExtrude","CAP_FACE",FACE,{"disambiguationData":[OSD([sQuery(id+"F18.wireOp",EDGE,"E61.bottom"),sQuery(id+"F18.wireOp",EDGE,"E61.top"),sQuery(id+"F18.wireOp",EDGE,"E61.left"),sQuery(id+"F18.wireOp",EDGE,"E61.right")])],"isStart":false});
            extrude(context, id + "F31", {"entities" : qUnion([Q0]), "operationType" : NewBodyOperationType.ADD, "endBound" : BoundingType.UP_TO_SURFACE, "depth" : 25 * mm, "endBoundEntityFace" : qUnion([Q1]), "offsetDistance" : 25 * mm});
        }
        {
            var Q0;
            Q0=makeQuery(id+"F28.opExtrude","CAP_FACE",FACE,{"disambiguationData":[OSD([sQuery(id+"F16.wireOp",EDGE,"E59.bottom"),sQuery(id+"F16.wireOp",EDGE,"E59.top"),sQuery(id+"F16.wireOp",EDGE,"E59.left"),sQuery(id+"F16.wireOp",EDGE,"E59.right")])],"isStart":false});
            var Q1;
            Q1=makeQuery(id+"F7.opExtrude","CAP_FACE",FACE,{"disambiguationData":[OSD([sQuery(id+"F6.wireOp",EDGE,"E45.bottom"),sQuery(id+"F6.wireOp",EDGE,"E45.top"),sQuery(id+"F6.wireOp",EDGE,"E45.left"),sQuery(id+"F6.wireOp",EDGE,"E45.right")])],"isStart":false});
            extrude(context, id + "F32", {"entities" : qUnion([Q0]), "endBound" : BoundingType.UP_TO_SURFACE, "depth" : 25 * mm, "endBoundEntityFace" : qUnion([Q1]), "offsetDistance" : 25 * mm});
        }
        {
            var Q0;
            Q0=makeQuery(id+"F32.opExtrude","CAP_FACE",FACE,{"disambiguationData":[OSD([sQuery(id+"F16.wireOp",EDGE,"E59.bottom"),sQuery(id+"F16.wireOp",EDGE,"E59.top"),sQuery(id+"F16.wireOp",EDGE,"E59.left"),sQuery(id+"F16.wireOp",EDGE,"E59.right")])],"isStart":false});
            var sketch = newSketch(context, id + "F33", { "sketchPlane" : qUnion([Q0])});
            skLineSegment(sketch, "E67.bottom", {"start": v(-9705, -2600) * mm, "end": v(-9435, -2600) * mm});
            skLineSegment(sketch, "E67.top", {"start": v(-9705, -1900) * mm, "end": v(-9435, -1900) * mm});
            skLineSegment(sketch, "E67.left", {"start": v(-9705, -1900) * mm, "end": v(-9705, -2600) * mm});
            skLineSegment(sketch, "E67.right", {"start": v(-9435, -1900) * mm, "end": v(-9435, -2600) * mm});
            skLineSegment(sketch, "E68", {"start": v(-9570, -1900) * mm, "end": v(-9570, -2600) * mm, "construction": true});
            skSolve(sketch);
        }
        {
            var Q0;
            Q0 = qSketchRegion(id + "F33", true);
            var Q1;
            Q1=makeQuery(id+"F25.opExtrude","CAP_FACE",FACE,{"disambiguationData":[OSD([sQuery(id+"F24.wireOp",EDGE,"E65.bottom"),sQuery(id+"F24.wireOp",EDGE,"E65.top"),sQuery(id+"F24.wireOp",EDGE,"E65.left"),sQuery(id+"F24.wireOp",EDGE,"E65.right")])],"isStart":false});
            extrude(context, id + "F34", {"entities" : qUnion([Q0]), "endBound" : BoundingType.UP_TO_SURFACE, "depth" : 25 * mm, "endBoundEntityFace" : qUnion([Q1]), "offsetDistance" : 25 * mm});
        }
        {
            var Q0;
            Q0=makeQuery(id+"F34.opExtrude","CAP_FACE",FACE,{"disambiguationData":[OSD([sQuery(id+"F33.wireOp",EDGE,"E67.bottom"),sQuery(id+"F33.wireOp",EDGE,"E67.top"),sQuery(id+"F33.wireOp",EDGE,"E67.left"),sQuery(id+"F33.wireOp",EDGE,"E67.right")])],"isStart":false});
            chamfer(context, id + "F35", {"entities" : qUnion([Q0]), "width" : 10 * mm, "tangentPropagation" : true});
        }
        {
            var Q0;
            {var subQ0=sQuery(id+"F0.wireOp",EDGE,"E34");var subQ1=sQuery(id+"F0.wireOp",EDGE,"E33");var subQ2=sQuery(id+"F0.wireOp",EDGE,"E32");var subQ3=sQuery(id+"F0.wireOp",EDGE,"E31");var subQ4=sQuery(id+"F0.wireOp",EDGE,"E30");var subQ5=sQuery(id+"F0.wireOp",EDGE,"E29");var subQ6=sQuery(id+"F0.wireOp",EDGE,"E28");var subQ7=sQuery(id+"F0.wireOp",EDGE,"E27");var subQ8=sQuery(id+"F0.wireOp",EDGE,"E26");var subQ9=sQuery(id+"F0.wireOp",EDGE,"E25");var subQ10=sQuery(id+"F0.wireOp",EDGE,"E24");var subQ11=sQuery(id+"F0.wireOp",EDGE,"E23");var subQ12=sQuery(id+"F0.wireOp",EDGE,"E15");var subQ13=sQuery(id+"F0.wireOp",EDGE,"E14");var subQ14=sQuery(id+"F0.wireOp",EDGE,"E10");var subQ15=sQuery(id+"F0.wireOp",EDGE,"E9");var subQ16=sQuery(id+"F0.wireOp",EDGE,"E16");var subQ17=sQuery(id+"F0.wireOp",EDGE,"E17");var subQ18=sQuery(id+"F0.wireOp",EDGE,"E19");var subQ19=sQuery(id+"F0.wireOp",EDGE,"E20");var subQ20=sQuery(id+"F0.wireOp",EDGE,"E21");var subQ21=sQuery(id+"F0.wireOp",EDGE,"E22");var subQ22=sQuery(id+"F0.wireOp",EDGE,"E35");Q0=makeQuery(id+"F14.boolean.opBoolean","SPLIT",FACE,{"disambiguationData":[TD([makeQuery(id+"F5.opExtrude","SWEPT_FACE",FACE,{"disambiguationData":[OSD([subQ15])]})])],"derivedFrom":makeQuery(id+"F5.opExtrude","CAP_FACE",FACE,{"disambiguationData":[OSD([sQuery(id+"F0.wireOp",EDGE,"E2"),sQuery(id+"F0.wireOp",EDGE,"E3"),sQuery(id+"F0.wireOp",EDGE,"E4"),sQuery(id+"F0.wireOp",EDGE,"E5"),sQuery(id+"F0.wireOp",EDGE,"E6"),sQuery(id+"F0.wireOp",EDGE,"E7"),sQuery(id+"F0.wireOp",EDGE,"E8"),subQ15,subQ14,subQ13,subQ12,subQ16,subQ17,sQuery(id+"F0.wireOp",EDGE,"E18"),subQ18,subQ19,subQ20,subQ21,subQ11,subQ10,subQ9,subQ8,subQ7,subQ6,subQ5,subQ4,subQ3,subQ2,subQ1,subQ0,subQ22])],"isStart":true})});}
            var sketch = newSketch(context, id + "F36", { "sketchPlane" : qUnion([Q0])});
            skLineSegment(sketch, "E69.bottom", {"start": v(-9690, -420) * mm, "end": v(-8140, -420) * mm});
            skLineSegment(sketch, "E69.top", {"start": v(-9690, -500) * mm, "end": v(-8140, -500) * mm});
            skLineSegment(sketch, "E69.left", {"start": v(-9690, -420) * mm, "end": v(-9690, -500) * mm});
            skLineSegment(sketch, "E69.right", {"start": v(-8140, -420) * mm, "end": v(-8140, -500) * mm});
            skSolve(sketch);
        }
        {
            var Q0;
            Q0 = qSketchRegion(id + "F36", true);
            extrude(context, id + "F37", {"entities" : qUnion([Q0]), "depth" : 50 * mm, "offsetDistance" : 25 * mm, "hasSecondDirection" : true, "secondDirectionOppositeDirection" : true, "secondDirectionDepth" : 150 * mm});
        }
        {
            var Q0;
            Q0=makeQuery(id+"F25.opExtrude","CAP_FACE",FACE,{"disambiguationData":[OSD([sQuery(id+"F24.wireOp",EDGE,"E65.bottom"),sQuery(id+"F24.wireOp",EDGE,"E65.top"),sQuery(id+"F24.wireOp",EDGE,"E65.left"),sQuery(id+"F24.wireOp",EDGE,"E65.right")])],"isStart":false});
            var sketch = newSketch(context, id + "F38", { "sketchPlane" : qUnion([Q0])});
            skLineSegment(sketch, "E70.bottom", {"start": v(-9610, -1770) * mm, "end": v(-9530, -1770) * mm});
            skLineSegment(sketch, "E70.top", {"start": v(-9610, -1850) * mm, "end": v(-9530, -1850) * mm});
            skLineSegment(sketch, "E70.left", {"start": v(-9610, -1770) * mm, "end": v(-9610, -1850) * mm});
            skLineSegment(sketch, "E70.right", {"start": v(-9530, -1770) * mm, "end": v(-9530, -1850) * mm});
            skLineSegment(sketch, "E71.bottom", {"start": v(-9610, -650) * mm, "end": v(-9530, -650) * mm});
            skLineSegment(sketch, "E71.top", {"start": v(-9610, -730) * mm, "end": v(-9530, -730) * mm});
            skLineSegment(sketch, "E71.left", {"start": v(-9610, -650) * mm, "end": v(-9610, -730) * mm});
            skLineSegment(sketch, "E71.right", {"start": v(-9530, -650) * mm, "end": v(-9530, -730) * mm});
            skLineSegment(sketch, "E72", {"start": v(-9610, -1810) * mm, "end": v(-9530, -1810) * mm, "construction": true});
            skLineSegment(sketch, "E73", {"start": v(-9610, -690) * mm, "end": v(-9530, -690) * mm, "construction": true});
            skLineSegment(sketch, "E74", {"start": v(-9570, -690) * mm, "end": v(-9570, -1810) * mm, "construction": true});
            skLineSegment(sketch, "E75", {"start": v(-9570, -1850) * mm, "end": v(-9570, -1900) * mm, "construction": true});
            skSolve(sketch);
        }
        {
            var Q0;
            Q0 = qSketchRegion(id + "F38", true);
            extrude(context, id + "F39", {"entities" : qUnion([Q0]), "depth" : 800 * mm, "offsetDistance" : 25 * mm, "hasSecondDirection" : true, "secondDirectionOppositeDirection" : true, "secondDirectionDepth" : 150 * mm});
        }
        {
            var Q0;
            Q0=makeQuery(id+"F25.opExtrude","CAP_FACE",FACE,{"disambiguationData":[OSD([sQuery(id+"F24.wireOp",EDGE,"E65.bottom"),sQuery(id+"F24.wireOp",EDGE,"E65.top"),sQuery(id+"F24.wireOp",EDGE,"E65.left"),sQuery(id+"F24.wireOp",EDGE,"E65.right")])],"isStart":false});
            var sketch = newSketch(context, id + "F40", { "sketchPlane" : qUnion([Q0])});
            skLineSegment(sketch, "E76.bottom", {"start": v(-9585, -7795) * mm, "end": v(-9555, -7795) * mm});
            skLineSegment(sketch, "E76.top", {"start": v(-9585, -7825) * mm, "end": v(-9555, -7825) * mm});
            skLineSegment(sketch, "E76.left", {"start": v(-9585, -7795) * mm, "end": v(-9585, -7825) * mm});
            skLineSegment(sketch, "E76.right", {"start": v(-9555, -7795) * mm, "end": v(-9555, -7825) * mm});
            skLineSegment(sketch, "E77.bottom", {"start": v(-9585, -6295) * mm, "end": v(-9555, -6295) * mm});
            skLineSegment(sketch, "E77.top", {"start": v(-9585, -6325) * mm, "end": v(-9555, -6325) * mm});
            skLineSegment(sketch, "E77.left", {"start": v(-9585, -6295) * mm, "end": v(-9585, -6325) * mm});
            skLineSegment(sketch, "E77.right", {"start": v(-9555, -6295) * mm, "end": v(-9555, -6325) * mm});
            skLineSegment(sketch, "E78", {"start": v(-9585, -7810) * mm, "end": v(-9555, -7810) * mm, "construction": true});
            skLineSegment(sketch, "E79", {"start": v(-9585, -6310) * mm, "end": v(-9555, -6310) * mm, "construction": true});
            skLineSegment(sketch, "E80", {"start": v(-9570, -6310) * mm, "end": v(-9570, -7810) * mm, "construction": true});
            skLineSegment(sketch, "E81", {"start": v(-9570, -7810) * mm, "end": v(-9570, -8150) * mm, "construction": true});
            skLineSegment(sketch, "E82.bottom", {"start": v(-9585, -4795) * mm, "end": v(-9555, -4795) * mm});
            skLineSegment(sketch, "E82.top", {"start": v(-9585, -4825) * mm, "end": v(-9555, -4825) * mm});
            skLineSegment(sketch, "E82.left", {"start": v(-9585, -4795) * mm, "end": v(-9585, -4825) * mm});
            skLineSegment(sketch, "E82.right", {"start": v(-9555, -4795) * mm, "end": v(-9555, -4825) * mm});
            skLineSegment(sketch, "E83.bottom", {"start": v(-9585, -3295) * mm, "end": v(-9555, -3295) * mm});
            skLineSegment(sketch, "E83.top", {"start": v(-9585, -3325) * mm, "end": v(-9555, -3325) * mm});
            skLineSegment(sketch, "E83.left", {"start": v(-9585, -3295) * mm, "end": v(-9585, -3325) * mm});
            skLineSegment(sketch, "E83.right", {"start": v(-9555, -3295) * mm, "end": v(-9555, -3325) * mm});
            skLineSegment(sketch, "E84", {"start": v(-9585, -3310) * mm, "end": v(-9555, -3310) * mm, "construction": true});
            skLineSegment(sketch, "E85", {"start": v(-9585, -4810) * mm, "end": v(-9555, -4810) * mm, "construction": true});
            skLineSegment(sketch, "E86", {"start": v(-9570, -6310) * mm, "end": v(-9570, -4810) * mm, "construction": true});
            skLineSegment(sketch, "E87", {"start": v(-9570, -4810) * mm, "end": v(-9570, -3310) * mm, "construction": true});
            skLineSegment(sketch, "E88", {"start": v(-9570, -3310) * mm, "end": v(-9570, -1810) * mm, "construction": true});
            skSolve(sketch);
        }
        {
            var Q0;
            Q0 = qSketchRegion(id + "F40", true);
            extrude(context, id + "F41", {"entities" : qUnion([Q0]), "depth" : 850 * mm, "offsetDistance" : 25 * mm});
        }
        {
            var Q0;
            {var subQ1=sQuery(id+"F13.wireOp",EDGE,"E53.top");Q0=makeQuery(id+"F13.imprint","IMPRINT",FACE,{"disambiguationData":[TD([[makeQuery(id+"F13.imprint","IMPRINT",EDGE,{"derivedFrom":subQ1}),-1.0]])]});}
            var sketch = newSketch(context, id + "F42", { "sketchPlane" : qUnion([Q0])});
            skLineSegment(sketch, "E89.0.0", {"start": v(-8140, -500) * mm, "end": v(-9690, -500) * mm});
            skLineSegment(sketch, "E89.0.1", {"start": v(-9690, -500) * mm, "end": v(-9690, -1900) * mm});
            skLineSegment(sketch, "E89.0.13", {"start": v(0, -7850) * mm, "end": v(0, -5750) * mm});
            skLineSegment(sketch, "E89.0.14", {"start": v(0, -5750) * mm, "end": v(-100, -5750) * mm});
            skLineSegment(sketch, "E89.0.15", {"start": v(-100, -5750) * mm, "end": v(-100, -5350) * mm});
            skLineSegment(sketch, "E89.0.16", {"start": v(-100, -5350) * mm, "end": v(0, -5350) * mm});
            skLineSegment(sketch, "E89.0.17", {"start": v(0, -5350) * mm, "end": v(0, -3330) * mm});
            skLineSegment(sketch, "E89.0.18", {"start": v(0, -3330) * mm, "end": v(-150, -3330) * mm});
            skLineSegment(sketch, "E89.0.19", {"start": v(-150, -3330) * mm, "end": v(-150, -3282) * mm});
            skLineSegment(sketch, "E89.0.20", {"start": v(-150, -3282) * mm, "end": v(-3390, -3282) * mm});
            skLineSegment(sketch, "E89.0.21", {"start": v(-3390, -3282) * mm, "end": v(-3390, -1650) * mm});
            skLineSegment(sketch, "E89.0.22", {"start": v(-3390, -1650) * mm, "end": v(-6390, -1650) * mm});
            skLineSegment(sketch, "E89.0.23", {"start": v(-6390, -1650) * mm, "end": v(-6390, -2000) * mm});
            skLineSegment(sketch, "E89.0.24", {"start": v(-6390, -2000) * mm, "end": v(-8140, -2000) * mm});
            skLineSegment(sketch, "E89.0.25", {"start": v(-8140, -2000) * mm, "end": v(-8140, -500) * mm});
            skLineSegment(sketch, "E90", {"start": v(-8950, -1900) * mm, "end": v(-8950, -7850) * mm});
            skLineSegment(sketch, "E91", {"start": v(-8950, -7850) * mm, "end": v(0, -7850) * mm});
            skLineSegment(sketch, "E92", {"start": v(-9690, -1900) * mm, "end": v(-8950, -1900) * mm});
            skSolve(sketch);
        }
        {
            var Q0;
            Q0 = qSketchRegion(id + "F42", true);
            extrude(context, id + "F43", {"entities" : qUnion([Q0]), "depth" : 40 * mm, "offsetDistance" : 25 * mm});
        }
        {
            var Q0;
            {var subQ0=sQuery(id+"F24.wireOp",EDGE,"E65.right");var subQ1=sQuery(id+"F24.wireOp",EDGE,"E65.left");var subQ2=sQuery(id+"F24.wireOp",EDGE,"E65.top");var subQ3=sQuery(id+"F24.wireOp",EDGE,"E65.bottom");var subQ4=makeQuery(id+"F25.opExtrude","CAP_FACE",FACE,{"disambiguationData":[OSD([subQ3,subQ2,subQ1,subQ0])],"isStart":false});Q0=makeQuery(id+"F38.imprint","IMPRINT",FACE,{"disambiguationData":[TD([[makeQuery(id+"F38.imprint","IMPRINT",EDGE,{"derivedFrom":makeQuery(id+"F26.opChamfer","BLEND_EDGE",EDGE,{"blendedFrom":[makeQuery(id+"F25.opExtrude","CAP_EDGE",EDGE,{"disambiguationData":[OSD([subQ3])],"isStart":false}),subQ4],"blendedInto":[subQ4]})}),1.0]])]});}
            var sketch = newSketch(context, id + "F44", { "sketchPlane" : qUnion([Q0])});
            skLineSegment(sketch, "E93.bottom", {"start": v(-9585, -185) * mm, "end": v(-9555, -185) * mm});
            skLineSegment(sketch, "E93.top", {"start": v(-9585, -215) * mm, "end": v(-9555, -215) * mm});
            skLineSegment(sketch, "E93.left", {"start": v(-9585, -185) * mm, "end": v(-9585, -215) * mm});
            skLineSegment(sketch, "E93.right", {"start": v(-9555, -185) * mm, "end": v(-9555, -215) * mm});
            skLineSegment(sketch, "E94", {"start": v(-9585, -200) * mm, "end": v(-9555, -200) * mm, "construction": true});
            skLineSegment(sketch, "E95", {"start": v(-9570, -200) * mm, "end": v(-9570, -690) * mm, "construction": true});
            skSolve(sketch);
        }
        {
            var Q0;
            Q0 = qSketchRegion(id + "F44", true);
            extrude(context, id + "F45", {"entities" : qUnion([Q0]), "depth" : 800 * mm, "offsetDistance" : 25 * mm, "hasSecondDirection" : true, "secondDirectionOppositeDirection" : true, "secondDirectionDepth" : 150 * mm});
        }
        {
            var Q0;
            Q0=makeQuery(id+"F15.boolean.opBoolean","COPY",FACE,{"derivedFrom":makeQuery(id+"F15.opExtrude","CAP_FACE",FACE,{"disambiguationData":[OSD([sQuery(id+"F0.wireOp",EDGE,"E2"),sQuery(id+"F0.wireOp",EDGE,"E3"),sQuery(id+"F0.wireOp",EDGE,"E4"),sQuery(id+"F0.wireOp",EDGE,"E5"),sQuery(id+"F0.wireOp",EDGE,"E6"),sQuery(id+"F0.wireOp",EDGE,"E7"),sQuery(id+"F0.wireOp",EDGE,"E8"),sQuery(id+"F0.wireOp",EDGE,"E9"),sQuery(id+"F0.wireOp",EDGE,"E10"),sQuery(id+"F0.wireOp",EDGE,"E14"),sQuery(id+"F0.wireOp",EDGE,"E15"),sQuery(id+"F0.wireOp",EDGE,"E16"),sQuery(id+"F0.wireOp",EDGE,"E17"),sQuery(id+"F0.wireOp",EDGE,"E18"),sQuery(id+"F0.wireOp",EDGE,"E19"),sQuery(id+"F0.wireOp",EDGE,"E20"),sQuery(id+"F0.wireOp",EDGE,"E21"),sQuery(id+"F0.wireOp",EDGE,"E22"),sQuery(id+"F0.wireOp",EDGE,"E23"),sQuery(id+"F0.wireOp",EDGE,"E24"),sQuery(id+"F0.wireOp",EDGE,"E25"),sQuery(id+"F0.wireOp",EDGE,"E26"),sQuery(id+"F0.wireOp",EDGE,"E27"),sQuery(id+"F0.wireOp",EDGE,"E28"),sQuery(id+"F0.wireOp",EDGE,"E29"),sQuery(id+"F0.wireOp",EDGE,"E30"),sQuery(id+"F0.wireOp",EDGE,"E31"),sQuery(id+"F0.wireOp",EDGE,"E32"),sQuery(id+"F0.wireOp",EDGE,"E33"),sQuery(id+"F0.wireOp",EDGE,"E34"),sQuery(id+"F0.wireOp",EDGE,"E35")])],"isStart":false})});
            var sketch = newSketch(context, id + "F46", { "sketchPlane" : qUnion([Q0])});
            skLineSegment(sketch, "E96.bottom", {"start": v(-9690, 0) * mm, "end": v(-8140, 0) * mm});
            skLineSegment(sketch, "E96.top", {"start": v(-9690, -420) * mm, "end": v(-8140, -420) * mm});
            skLineSegment(sketch, "E96.left", {"start": v(-9690, 0) * mm, "end": v(-9690, -420) * mm});
            skLineSegment(sketch, "E96.right", {"start": v(-8140, 0) * mm, "end": v(-8140, -420) * mm});
            skSolve(sketch);
        }
        {
            var Q0;
            Q0 = qSketchRegion(id + "F46", true);
            extrude(context, id + "F47", {"entities" : qUnion([Q0]), "depth" : 130 * mm, "offsetDistance" : 25 * mm});
        }
        {
            var Q0;
            Q0=makeQuery(id+"F5.opExtrude","SWEPT_FACE",FACE,{"disambiguationData":[OSD([sQuery(id+"F0.wireOp",EDGE,"E19")])]});
            var sketch = newSketch(context, id + "F48", { "sketchPlane" : qUnion([Q0])});
            skLineSegment(sketch, "E97.0", {"start": v(360, -250) * mm, "end": v(360, -100) * mm});
            skLineSegment(sketch, "E97.1", {"start": v(360, -250) * mm, "end": v(560, -250) * mm});
            skLineSegment(sketch, "E97.2", {"start": v(560, -250) * mm, "end": v(560, 0) * mm});
            skLineSegment(sketch, "E97.3", {"start": v(500, 0) * mm, "end": v(560, 0) * mm});
            skLineSegment(sketch, "E97.4", {"start": v(500, 0) * mm, "end": v(500, -150) * mm});
            skLineSegment(sketch, "E97.5", {"start": v(420, -150) * mm, "end": v(500, -150) * mm});
            skLineSegment(sketch, "E97.6", {"start": v(420, -100) * mm, "end": v(420, -150) * mm});
            skLineSegment(sketch, "E97.7", {"start": v(360, -100) * mm, "end": v(420, -100) * mm});
            skPoint(sketch, "E98.orphan", {"position": v(0, -100) * mm});
            skPoint(sketch, "E99.orphan", {"position": v(420, 50) * mm});
            skPoint(sketch, "E100.orphan", {"position": v(500, 50) * mm});
            skPoint(sketch, "E101.orphan", {"position": v(1900, 0) * mm});
            skSolve(sketch);
        }
        {
            var Q0;
            Q0 = qSketchRegion(id + "F48", true);
            var Q1;
            Q1=makeQuery(id+"F5.opExtrude","SWEPT_FACE",FACE,{"disambiguationData":[OSD([sQuery(id+"F0.wireOp",EDGE,"E17")])]});
            extrude(context, id + "F49", {"entities" : qUnion([Q0]), "endBound" : BoundingType.UP_TO_SURFACE, "oppositeDirection" : true, "depth" : 25 * mm, "endBoundEntityFace" : qUnion([Q1]), "offsetDistance" : 25 * mm});
        }
        {
            var Q0;
            Q0=makeQuery(id+"F31.boolean.opBoolean","MERGE",FACE,{"derivedFrom":[makeQuery(id+"F30.opExtrude","CAP_FACE",FACE,{"disambiguationData":[OSD([sQuery(id+"F18.wireOp",EDGE,"E60.bottom"),sQuery(id+"F18.wireOp",EDGE,"E60.top"),sQuery(id+"F18.wireOp",EDGE,"E60.left"),sQuery(id+"F18.wireOp",EDGE,"E60.right")])],"isStart":false}),makeQuery(id+"F30.opExtrude","CAP_FACE",FACE,{"disambiguationData":[OSD([sQuery(id+"F18.wireOp",EDGE,"E61.bottom"),sQuery(id+"F18.wireOp",EDGE,"E61.top"),sQuery(id+"F18.wireOp",EDGE,"E61.left"),sQuery(id+"F18.wireOp",EDGE,"E61.right")])],"isStart":false}),makeQuery(id+"F31.opExtrude","CAP_FACE",FACE,{"disambiguationData":[OSD([sQuery(id+"F20.wireOp",EDGE,"E62.bottom"),sQuery(id+"F20.wireOp",EDGE,"E62.top"),sQuery(id+"F20.wireOp",EDGE,"E62.left"),sQuery(id+"F20.wireOp",EDGE,"E62.right")])],"isStart":false})]});
            var Q1;
            {var subQ0=sQuery(id+"F0.wireOp",EDGE,"E34");var subQ1=sQuery(id+"F0.wireOp",EDGE,"E33");var subQ2=sQuery(id+"F0.wireOp",EDGE,"E32");var subQ3=sQuery(id+"F0.wireOp",EDGE,"E31");var subQ4=sQuery(id+"F0.wireOp",EDGE,"E30");var subQ5=sQuery(id+"F0.wireOp",EDGE,"E29");var subQ6=sQuery(id+"F0.wireOp",EDGE,"E28");var subQ7=sQuery(id+"F0.wireOp",EDGE,"E27");var subQ8=sQuery(id+"F0.wireOp",EDGE,"E26");var subQ9=sQuery(id+"F0.wireOp",EDGE,"E25");var subQ10=sQuery(id+"F0.wireOp",EDGE,"E24");var subQ11=sQuery(id+"F0.wireOp",EDGE,"E23");var subQ12=sQuery(id+"F0.wireOp",EDGE,"E15");var subQ13=sQuery(id+"F0.wireOp",EDGE,"E14");var subQ14=sQuery(id+"F0.wireOp",EDGE,"E10");var subQ15=sQuery(id+"F0.wireOp",EDGE,"E9");var subQ16=sQuery(id+"F0.wireOp",EDGE,"E16");var subQ17=sQuery(id+"F0.wireOp",EDGE,"E17");var subQ18=sQuery(id+"F0.wireOp",EDGE,"E19");var subQ19=sQuery(id+"F0.wireOp",EDGE,"E20");var subQ20=sQuery(id+"F0.wireOp",EDGE,"E21");var subQ21=sQuery(id+"F0.wireOp",EDGE,"E22");var subQ22=sQuery(id+"F0.wireOp",EDGE,"E35");Q1=makeQuery(id+"F14.boolean.opBoolean","SPLIT",FACE,{"disambiguationData":[TD([makeQuery(id+"F5.opExtrude","SWEPT_FACE",FACE,{"disambiguationData":[OSD([subQ15])]})])],"derivedFrom":makeQuery(id+"F5.opExtrude","CAP_FACE",FACE,{"disambiguationData":[OSD([sQuery(id+"F0.wireOp",EDGE,"E2"),sQuery(id+"F0.wireOp",EDGE,"E3"),sQuery(id+"F0.wireOp",EDGE,"E4"),sQuery(id+"F0.wireOp",EDGE,"E5"),sQuery(id+"F0.wireOp",EDGE,"E6"),sQuery(id+"F0.wireOp",EDGE,"E7"),sQuery(id+"F0.wireOp",EDGE,"E8"),subQ15,subQ14,subQ13,subQ12,subQ16,subQ17,sQuery(id+"F0.wireOp",EDGE,"E18"),subQ18,subQ19,subQ20,subQ21,subQ11,subQ10,subQ9,subQ8,subQ7,subQ6,subQ5,subQ4,subQ3,subQ2,subQ1,subQ0,subQ22])],"isStart":true})});}
            extrude(context, id + "F50", {"entities" : qUnion([Q0]), "endBound" : BoundingType.UP_TO_SURFACE, "depth" : 25 * mm, "endBoundEntityFace" : qUnion([Q1]), "offsetDistance" : 25 * mm});
        }
        {
            var Q0;
            {var subQ0=sQuery(id+"F0.wireOp",EDGE,"E34");var subQ1=sQuery(id+"F0.wireOp",EDGE,"E33");var subQ2=sQuery(id+"F0.wireOp",EDGE,"E32");var subQ3=sQuery(id+"F0.wireOp",EDGE,"E31");var subQ4=sQuery(id+"F0.wireOp",EDGE,"E30");var subQ5=sQuery(id+"F0.wireOp",EDGE,"E29");var subQ6=sQuery(id+"F0.wireOp",EDGE,"E28");var subQ7=sQuery(id+"F0.wireOp",EDGE,"E27");var subQ8=sQuery(id+"F0.wireOp",EDGE,"E26");var subQ9=sQuery(id+"F0.wireOp",EDGE,"E25");var subQ10=sQuery(id+"F0.wireOp",EDGE,"E24");var subQ11=sQuery(id+"F0.wireOp",EDGE,"E23");var subQ12=sQuery(id+"F0.wireOp",EDGE,"E15");var subQ13=sQuery(id+"F0.wireOp",EDGE,"E14");var subQ14=sQuery(id+"F0.wireOp",EDGE,"E10");var subQ15=sQuery(id+"F0.wireOp",EDGE,"E9");var subQ16=sQuery(id+"F0.wireOp",EDGE,"E16");var subQ17=sQuery(id+"F0.wireOp",EDGE,"E17");var subQ18=sQuery(id+"F0.wireOp",EDGE,"E19");var subQ19=sQuery(id+"F0.wireOp",EDGE,"E20");var subQ20=sQuery(id+"F0.wireOp",EDGE,"E21");var subQ21=sQuery(id+"F0.wireOp",EDGE,"E22");var subQ22=sQuery(id+"F0.wireOp",EDGE,"E35");Q0=makeQuery(id+"F14.boolean.opBoolean","SPLIT",FACE,{"disambiguationData":[TD([makeQuery(id+"F5.opExtrude","SWEPT_FACE",FACE,{"disambiguationData":[OSD([subQ15])]})])],"derivedFrom":makeQuery(id+"F5.opExtrude","CAP_FACE",FACE,{"disambiguationData":[OSD([sQuery(id+"F0.wireOp",EDGE,"E2"),sQuery(id+"F0.wireOp",EDGE,"E3"),sQuery(id+"F0.wireOp",EDGE,"E4"),sQuery(id+"F0.wireOp",EDGE,"E5"),sQuery(id+"F0.wireOp",EDGE,"E6"),sQuery(id+"F0.wireOp",EDGE,"E7"),sQuery(id+"F0.wireOp",EDGE,"E8"),subQ15,subQ14,subQ13,subQ12,subQ16,subQ17,sQuery(id+"F0.wireOp",EDGE,"E18"),subQ18,subQ19,subQ20,subQ21,subQ11,subQ10,subQ9,subQ8,subQ7,subQ6,subQ5,subQ4,subQ3,subQ2,subQ1,subQ0,subQ22])],"isStart":true})});}
            var sketch = newSketch(context, id + "F51", { "sketchPlane" : qUnion([Q0])});
            skCircle(sketch, "E102", {"center": v(-8240, -700) * mm, "radius": 60 * mm});
            skCircle(sketch, "E103", {"center": v(-8240, -850) * mm, "radius": 60 * mm});
            skLineSegment(sketch, "E104", {"start": v(-8240, -700) * mm, "end": v(-8240, -850) * mm, "construction": true});
            skLineSegment(sketch, "E105", {"start": v(-8240, -700) * mm, "end": v(-8240, -500) * mm, "construction": true});
            skLineSegment(sketch, "E106", {"start": v(-8240, -700) * mm, "end": v(-8140, -700) * mm, "construction": true});
            skSolve(sketch);
        }
        {
            var Q0;
            Q0 = qSketchRegion(id + "F51", true);
            extrude(context, id + "F52", {"entities" : qUnion([Q0]), "depth" : 50 * mm, "offsetDistance" : 25 * mm});
        }
    });
